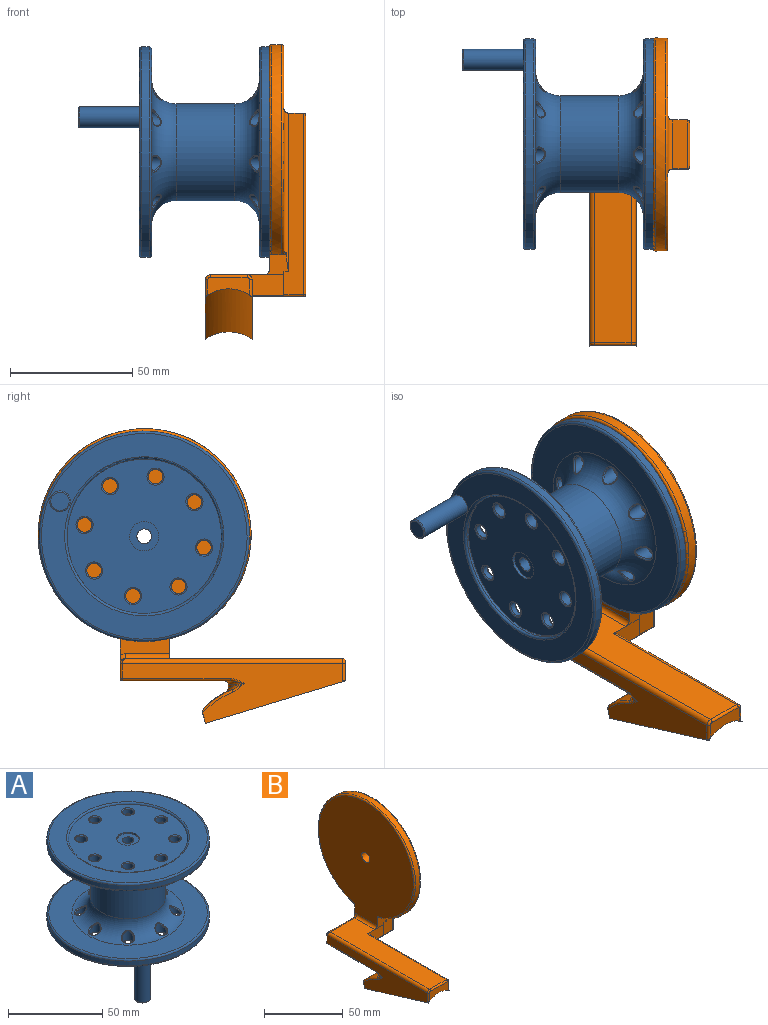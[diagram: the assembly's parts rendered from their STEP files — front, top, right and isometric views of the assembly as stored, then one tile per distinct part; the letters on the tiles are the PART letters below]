
ASSEMBLY  parts=2 mates=1
PART A: 74 faces, bbox 93.1x93.1x79 mm
  f0: cylinder r=3mm len=49mm, axis (0,0,-1), area 923.6mm2, adj f29,f32
  f1: plane 84x84mm, normal (0,0,-1), area 2166.7mm2, adj f27,f37,f70
  f2: cylinder r=43mm len=86mm, axis (0,0,-1), area 810.5mm2, adj f70,f71
  f3: plane 84x84mm, normal (0,0,1), area 2761.3mm2, adj f34,f71
  f4: cylinder r=19.75mm len=39.5mm, axis (0,0,-1), area 2978.2mm2, adj f34,f35
  f5: plane 84x84mm, normal (0,0,-1), area 2761.3mm2, adj f35,f72
  f6: cylinder r=43mm len=86mm, axis (0,0,-1), area 810.5mm2, adj f72,f73
  f7: plane 84x84mm, normal (0,0,1), area 2223.5mm2, adj f36,f73
  f8: cylinder r=31.5mm len=63mm, axis (0,0,-1), area 197.9mm2, adj f9,f37
  f9: plane 63x63mm, normal (0,0,-1), area 2696.3mm2, adj f8,f31,f38,f39,f40,f41,f42,f43
  f10: plane 63x63mm, normal (0,0,1), area 2696.3mm2, adj f30,f36,f46,f47,f48,f49,f50,f51
  f11: cylinder r=3mm len=7.27mm, axis (0,0,-1), area 87.2mm2, adj f53,f69
  f12: cylinder r=3mm len=7.27mm, axis (0,0,-1), area 87.2mm2, adj f52,f67
  f13: cylinder r=3mm len=7.27mm, axis (0,0,-1), area 87.2mm2, adj f51,f65
  f14: cylinder r=3mm len=7.27mm, axis (0,0,-1), area 87.2mm2, adj f50,f63
  f15: cylinder r=3mm len=7.27mm, axis (0,0,-1), area 87.2mm2, adj f49,f61
  f16: cylinder r=3mm len=7.27mm, axis (0,0,-1), area 87.2mm2, adj f48,f59
  f17: cylinder r=3mm len=7.27mm, axis (0,0,-1), area 87.2mm2, adj f47,f57
  f18: cylinder r=3mm len=7.27mm, axis (0,0,-1), area 87.2mm2, adj f46,f55
  f19: cylinder r=3mm len=6.27mm, axis (0,0,-1), area 68.4mm2, adj f38,f68
  f20: cylinder r=3mm len=6.27mm, axis (0,0,-1), area 68.3mm2, adj f39,f66
  f21: cylinder r=3mm len=6.27mm, axis (0,0,-1), area 68.3mm2, adj f40,f64
  f22: cylinder r=3mm len=6.27mm, axis (0,0,-1), area 68.4mm2, adj f41,f62
  f23: cylinder r=3mm len=6.27mm, axis (0,0,-1), area 68.4mm2, adj f42,f60
  f24: cylinder r=3mm len=6.27mm, axis (0,0,-1), area 68.3mm2, adj f43,f58
  f25: cylinder r=3mm len=6.27mm, axis (0,0,-1), area 68.3mm2, adj f44,f56
  f26: cylinder r=3mm len=6.27mm, axis (0,0,-1), area 68.4mm2, adj f45,f54
  f27: cylinder r=4.25mm len=24.5mm, axis (0,0,1), area 654.2mm2, adj f1,f33
  f28: plane 7.5x7.5mm, normal (0,0,-1), area 44.2mm2, adj f33
  f29: plane 12x12mm, normal (0,0,1), area 84.8mm2, adj f0,f30
  f30: cylinder r=6mm len=12mm, axis (0,0,1), area 37.7mm2, adj f10,f29
  f31: cylinder r=6mm len=12mm, axis (0,0,-1), area 37.7mm2, adj f9,f32
  f32: plane 12x12mm, normal (0,0,-1), area 84.8mm2, adj f0,f31
  f33: torus R=3.75mm, axis (0,0,-1), area 20.1mm2, adj f27,f28
  f34: torus R=29.75mm, axis (0,0,1), area 1960.6mm2, adj f3,f4,f54,f56,f58,f60,f62,f64
  f35: torus R=29.75mm, axis (0,0,1), area 1960.5mm2, adj f4,f5,f55,f57,f59,f61,f63,f65
  f36: torus R=32.5mm, axis (0,0,1), area 314.5mm2, adj f7,f10
  f37: torus R=32.5mm, axis (0,0,1), area 314.5mm2, adj f1,f8
  f38: torus R=3.5mm, axis (0,0,-1), area 15.7mm2, adj f9,f19
  f39: torus R=3.5mm, axis (0,0,-1), area 15.7mm2, adj f9,f20
  f40: torus R=3.5mm, axis (0,0,-1), area 15.7mm2, adj f9,f21
  f41: torus R=3.5mm, axis (0,0,-1), area 15.7mm2, adj f9,f22
  f42: torus R=3.5mm, axis (0,0,-1), area 15.7mm2, adj f9,f23
  f43: torus R=3.5mm, axis (0,0,-1), area 15.7mm2, adj f9,f24
  f44: torus R=3.5mm, axis (0,0,-1), area 15.7mm2, adj f9,f25
  f45: torus R=3.5mm, axis (0,0,-1), area 15.7mm2, adj f9,f26
  f46: torus R=3.5mm, axis (0,0,1), area 15.7mm2, adj f10,f18
  f47: torus R=3.5mm, axis (0,0,1), area 15.7mm2, adj f10,f17
  f48: torus R=3.5mm, axis (0,0,1), area 15.7mm2, adj f10,f16
  f49: torus R=3.5mm, axis (0,0,1), area 15.7mm2, adj f10,f15
  f50: torus R=3.5mm, axis (0,0,1), area 15.7mm2, adj f10,f14
  f51: torus R=3.5mm, axis (0,0,1), area 15.7mm2, adj f10,f13
  f52: torus R=3.5mm, axis (0,0,1), area 15.7mm2, adj f10,f12
  f53: torus R=3.5mm, axis (0,0,1), area 15.7mm2, adj f10,f11
  f54: bspline ~7.07x6.67mm, area 15.4mm2, adj f26,f34
  f55: bspline ~7.07x6.67mm, area 15.4mm2, adj f18,f35
  f56: bspline ~6.88x6.88mm, area 15.4mm2, adj f25,f34
  f57: bspline ~6.88x6.88mm, area 15.4mm2, adj f17,f35
  f58: bspline ~7.07x6.67mm, area 15.4mm2, adj f24,f34
  f59: bspline ~7.07x6.67mm, area 15.4mm2, adj f16,f35
  f60: bspline ~6.88x6.88mm, area 15.4mm2, adj f23,f34
  f61: bspline ~6.88x6.88mm, area 15.4mm2, adj f15,f35
  f62: bspline ~7.07x6.67mm, area 15.4mm2, adj f22,f34
  f63: bspline ~7.07x6.67mm, area 15.4mm2, adj f14,f35
  f64: bspline ~6.88x6.88mm, area 15.4mm2, adj f21,f34
  f65: bspline ~6.88x6.88mm, area 15.4mm2, adj f13,f35
  f66: bspline ~7.07x6.67mm, area 15.4mm2, adj f20,f34
  f67: bspline ~7.07x6.67mm, area 15.4mm2, adj f12,f35
  f68: bspline ~6.88x6.88mm, area 15.4mm2, adj f19,f34
  f69: bspline ~6.88x6.88mm, area 15.4mm2, adj f11,f35
  f70: torus R=42mm, axis (0,0,1), area 420.8mm2, adj f1,f2
  f71: torus R=42mm, axis (0,0,1), area 420.8mm2, adj f2,f3
  f72: torus R=42mm, axis (0,0,1), area 420.8mm2, adj f5,f6
  f73: torus R=42mm, axis (0,0,1), area 420.8mm2, adj f6,f7
PART B: 71 faces, bbox 43.3x130.7x124.6 mm
  f0: plane 1.22x0.23mm, normal (0,0,1), area 0.1mm2, adj f19,f24,f45
  f1: plane 19x3.53mm, normal (0,0.96,-0.29), area 28.8mm2, adj f19,f20,f24,f33
  f2: plane 9.8x0.05mm, normal (-1,0,0), area 0.5mm2, adj f5,f16,f18,f50
  f3: plane 2.46x0.02mm, normal (-1,0,0), area 0mm2, adj f8,f14,f15,f65
  f4: plane 20x6mm, normal (0,0,1), area 120mm2, adj f5,f8,f43,f53
  f5: plane 74x8mm, normal (0,-1,0), area 463mm2, adj f2,f4,f16,f44,f50,f51
  f6: plane 45.09x39.01mm, normal (0,0,-1), area 1138.2mm2, adj f20,f28,f30,f32,f50,f54,f58,f59
  f7: cylinder r=6mm len=12mm, axis (-1,0,0), area 18.8mm2, adj f9,f11
  f8: plane 74.75x39.75mm, normal (0,1,0), area 711.1mm2, adj f3,f4,f12,f14,f39,f41,f42,f55
  f9: plane 73x18mm, normal (1,0,0), area 1200.9mm2, adj f7,f51,f53,f54,f55
  f10: cylinder r=3.61mm len=14.5mm, axis (-1,0,0), area 328.8mm2, adj f11,f12
  f11: plane 12x12mm, normal (1,0,0), area 72.2mm2, adj f7,f10
  f12: plane 91.48x85mm, normal (-1,0,0), area 5761.6mm2, adj f8,f10,f14,f16,f40,f41,f70
  f13: plane 85x83.27mm, normal (1,0,0), area 4246.8mm2, adj f42,f43,f44,f64
  f14: plane 6.1x3.58mm, normal (0,1,0.01), area 14.9mm2, adj f3,f8,f12,f15,f70
  f15: cylinder r=43.5mm len=87mm, axis (1,0,0), area 1012.9mm2, adj f3,f14,f16,f63,f64,f65,f70
  f16: plane 10.27x9.47mm, normal (0,-1,-0.03), area 59.5mm2, adj f2,f5,f12,f15,f18,f40,f44,f63
  f17: plane 88.95x22mm, normal (0,0,1), area 1459.9mm2, adj f18,f37,f38,f39,f40,f49
  f18: plane 15x8.32mm, normal (0,-1,0), area 109mm2, adj f2,f16,f17,f20,f37,f50
  f19: plane 91.17x24.37mm, normal (-1,0,0), area 985.5mm2, adj f0,f1,f24,f33,f38,f45,f56,f58
  f20: plane 73.57x24.77mm, normal (1,0,0), area 900.3mm2, adj f1,f6,f18,f22,f24,f28,f33,f37
  f21: plane 17x7.34mm, normal (0,-1,0), area 94.4mm2, adj f24,f45,f46,f47,f48,f49
  f22: plane 1.22x0.23mm, normal (0,0,1), area 0.1mm2, adj f20,f24,f46
  f23: plane 3x1.32mm, normal (0,1,0), area 4mm2, adj f25,f26,f29,f30
  f24: cylinder r=15.77mm len=58.89mm, axis (0,0.96,-0.29), area 1228mm2, adj f0,f1,f19,f20,f21,f22,f45,f46
  f25: bspline ~8x8mm, area 5.5mm2, adj f23,f27,f28
  f26: bspline ~8x8mm, area 5.5mm2, adj f23,f31,f32
  f27: bspline ~10.3x8.05mm, area 18.3mm2, adj f25,f28,f29,f36,f67
  f28: bspline ~12.63x8.75mm, area 25.6mm2, adj f6,f20,f25,f27,f30,f67
  f29: cylinder r=1.6mm len=3mm, axis (-1,0,0), area 5.3mm2, adj f23,f27,f31,f35
  f30: cylinder r=1.6mm len=3mm, axis (-1,0,0), area 7.5mm2, adj f6,f23,f28,f32
  f31: bspline ~10.3x8.05mm, area 18.3mm2, adj f26,f29,f32,f34,f69
  f32: bspline ~12.57x7.98mm, area 22.9mm2, adj f6,f26,f30,f31,f56,f69
  f33: cylinder r=3.3mm len=19mm, axis (1,0,0), area 53.1mm2, adj f1,f19,f20,f34,f35,f36,f66,f68
  f34: bspline ~14.98x9.62mm, area 82.4mm2, adj f31,f33,f35,f68
  f35: cylinder r=34.1mm len=8.98mm, axis (-1,0,0), area 33.6mm2, adj f29,f33,f34,f36
  f36: bspline ~14.98x9.62mm, area 82.4mm2, adj f27,f33,f35,f66
  f37: cylinder r=2mm len=71mm, axis (0,1,0), area 223.1mm2, adj f17,f18,f20,f48
  f38: cylinder r=2mm len=89.95mm, axis (0,1,0), area 281mm2, adj f17,f19,f47,f62
  f39: cylinder r=2mm len=23mm, axis (1,0,0), area 70.7mm2, adj f8,f17,f41,f62
  f40: cylinder r=2mm len=18.02mm, axis (0,-1,0), area 56.5mm2, adj f12,f16,f17,f41
  f41: torus R=4mm, axis (1,0,0), area 8.4mm2, adj f8,f12,f39,f40
  f42: cylinder r=2mm len=59.09mm, axis (0,0,1), area 181.3mm2, adj f8,f13,f43,f65
  f43: cylinder r=2mm len=24mm, axis (0,-1,0), area 69.1mm2, adj f4,f13,f42,f44
  f44: cylinder r=2mm len=66.52mm, axis (0,0,-1), area 186.7mm2, adj f5,f13,f16,f43,f63
  f45: cylinder r=1mm len=7mm, axis (0,0,-1), area 10.7mm2, adj f0,f19,f21,f24,f47
  f46: cylinder r=1mm len=7mm, axis (0,0,-1), area 10.7mm2, adj f20,f21,f22,f24,f48
  f47: torus R=1mm, axis (0,-1,0), area 4mm2, adj f21,f38,f45,f49
  f48: torus R=1mm, axis (0,-1,0), area 4mm2, adj f21,f37,f46,f49
  f49: cylinder r=1mm len=15mm, axis (1,0,0), area 23.6mm2, adj f17,f21,f47,f48
  f50: cylinder r=1mm len=21mm, axis (-1,0,0), area 28.8mm2, adj f2,f5,f6,f18,f20,f52
  f51: cylinder r=1mm len=74mm, axis (0,0,1), area 115.5mm2, adj f5,f9,f52,f53
  f52: sphere r=1mm, area 1.6mm2, adj f50,f51,f54
  f53: cylinder r=1mm len=20mm, axis (0,1,0), area 29.8mm2, adj f4,f9,f51,f55
  f54: cylinder r=1mm len=18mm, axis (0,-1,0), area 28.3mm2, adj f6,f9,f52,f57
  f55: cylinder r=1mm len=74mm, axis (0,0,-1), area 115.5mm2, adj f8,f9,f53,f57
  f56: bspline ~6.96x2.37mm, area 5.2mm2, adj f19,f32,f58,f69
  f57: sphere r=1mm, area 1mm2, adj f54,f55,f59
  f58: cylinder r=1mm len=43.91mm, axis (0,1,0), area 69mm2, adj f6,f19,f56,f60
  f59: cylinder r=1mm len=39mm, axis (1,0,0), area 61.3mm2, adj f6,f8,f57,f60
  f60: sphere r=1mm, area 2.1mm2, adj f58,f59,f61
  f61: cylinder r=1mm len=6mm, axis (0,0,1), area 9.4mm2, adj f8,f19,f60,f62
  f62: bspline ~2.39x2mm, area 2.2mm2, adj f38,f39,f61
  f63: bspline ~3.65x2.39mm, area 3.3mm2, adj f15,f16,f44,f64
  f64: torus R=42.5mm, axis (1,0,0), area 386.9mm2, adj f13,f15,f63,f65
  f65: bspline ~3.79x3.58mm, area 4.1mm2, adj f3,f8,f15,f42,f64
  f66: bspline ~18.92x13.24mm, area 22.4mm2, adj f20,f33,f36,f67
  f67: bspline ~5.2x3.79mm, area 4.7mm2, adj f20,f27,f28,f66
  f68: bspline ~18.89x13.21mm, area 22.4mm2, adj f19,f33,f34,f69
  f69: bspline ~5.67x4.11mm, area 4.7mm2, adj f19,f31,f32,f56,f68
  f70: torus R=42.5mm, axis (1,0,0), area 393.6mm2, adj f12,f14,f15,f16
PLACE A rot(axis=(-0.66,0.35,-0.66),141.4deg) t=(-68.91,14.17,50.66)mm
PLACE B t=(-36.91,14.02,-8.34)mm fixed
MATE revolute B.f7 <-> A.f36  axis (-1,0,0) through (-42.91,14.17,50.66)mm
